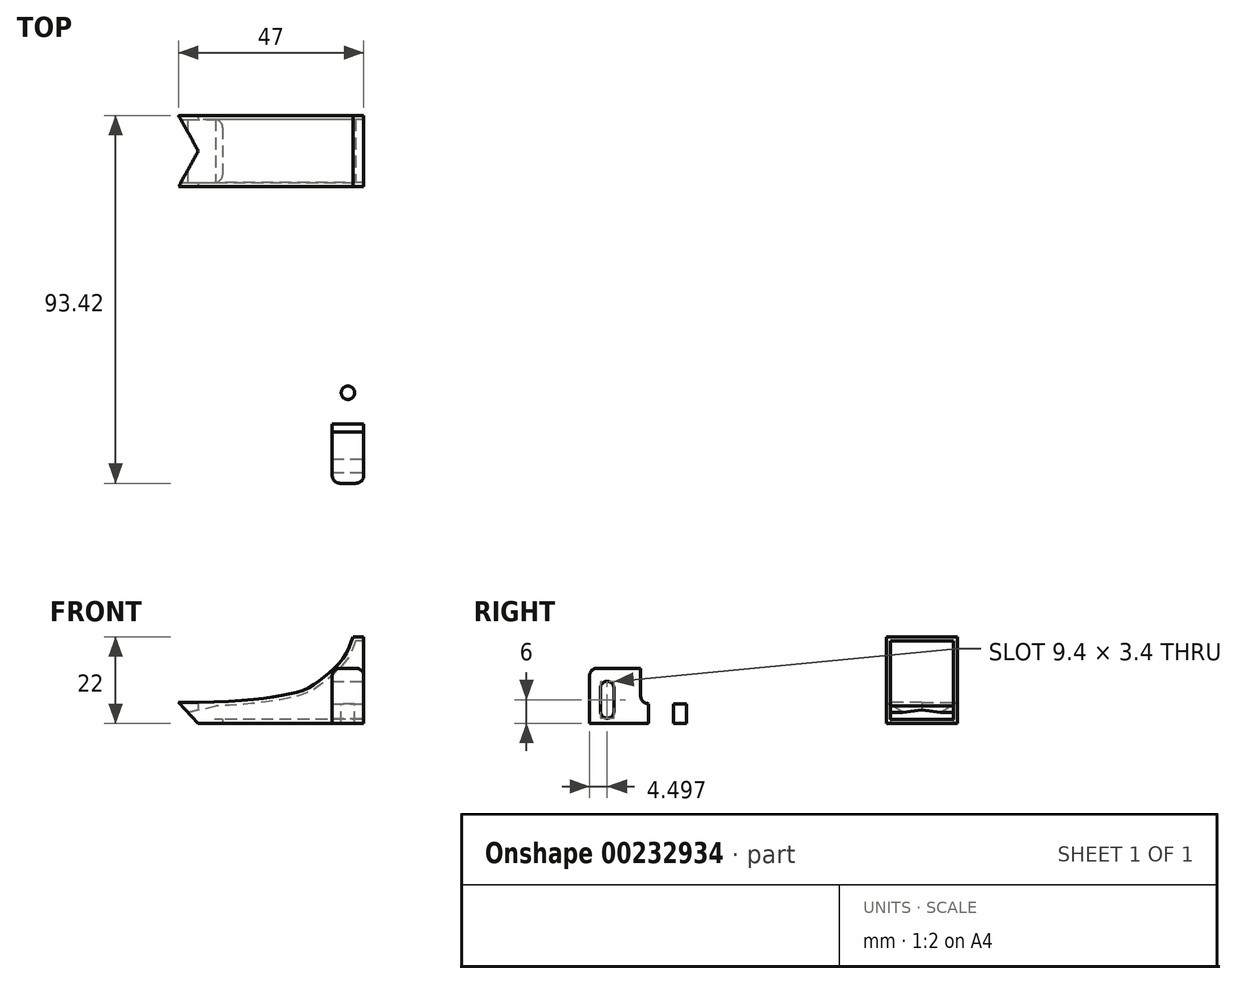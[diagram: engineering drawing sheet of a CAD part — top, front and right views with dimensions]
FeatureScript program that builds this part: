
annotation { "Feature Type Name" : "Feature", "Feature Type Description" : "" }
export const myFeature = defineFeature(function(context is Context, id is Id, definition is map)
    precondition{}
    {
        {
            var Q0;
            Q0=qCreatedBy(makeId("Top.planeOp"),FACE);
            var sketch = newSketch(context, id + "F0", { "sketchPlane" : qUnion([Q0])});
            skLineSegment(sketch, "E0.bottom", {"start": v(0, 0) * mm, "end": v(-47, 0) * mm});
            skLineSegment(sketch, "E0.top", {"start": v(0, 18) * mm, "end": v(-47, 18) * mm});
            skLineSegment(sketch, "E0.left", {"start": v(0, 0) * mm, "end": v(0, 18) * mm});
            skLineSegment(sketch, "E0.right", {"start": v(-47, 0) * mm, "end": v(-47, 18) * mm});
            skSolve(sketch);
        }
        {
            var Q0;
            Q0=makeQuery(id+"F0.imprint","IMPRINT",FACE,{"disambiguationData":[TD([[makeQuery(id+"F0.imprint","IMPRINT",EDGE,{"derivedFrom":sQuery(id+"F0.wireOp",EDGE,"E0.bottom")}),-1.0]])]});
            extrude(context, id + "F1", {"entities" : qUnion([Q0]), "depth" : 22 * mm});
        }
        {
            var Q0;
            Q0=makeQuery(id+"F1.opExtrude","SWEPT_FACE",FACE,{"disambiguationData":[OSD([sQuery(id+"F0.wireOp",EDGE,"E0.left")])]});
            var sketch = newSketch(context, id + "F2", { "sketchPlane" : qUnion([Q0])});
            skLineSegment(sketch, "E1.0", {"start": v(1, 21) * mm, "end": v(1, 1) * mm});
            skLineSegment(sketch, "E1.1", {"start": v(1, 21) * mm, "end": v(17, 21) * mm});
            skLineSegment(sketch, "E1.2", {"start": v(17, 21) * mm, "end": v(17, 1) * mm});
            skLineSegment(sketch, "E1.3", {"start": v(1, 1) * mm, "end": v(17, 1) * mm});
            skSolve(sketch);
        }
        {
            var Q0;
            Q0=makeQuery(id+"F1.opExtrude","SWEPT_FACE",FACE,{"disambiguationData":[OSD([sQuery(id+"F0.wireOp",EDGE,"E0.bottom")])]});
            var sketch = newSketch(context, id + "F3", { "sketchPlane" : qUnion([Q0])});
            skFitSpline(sketch, "E2", {"points": [v(-2.69, 22) * mm, v(-4.67, 17.3) * mm, v(-9.36, 12.4) * mm, v(-14.06, 9) * mm, v(-21.54, 6.98) * mm, v(-47, 5.31) * mm], "startDerivative": vector(-11.82, -27.31) * mm, "endDerivative": vector(-115.84, 1.02) * mm});
            skLineSegment(sketch, "E3", {"start": v(-47, 5.31) * mm, "end": v(-42, 0) * mm});
            skSolve(sketch);
        }
        {
            var Q0;
            {var subQ0=sQuery(id+"F3.wireOp",EDGE,"E2");Q0=makeQuery(id+"F3.imprint","IMPRINT",FACE,{"disambiguationData":[TD([[makeQuery(id+"F3.imprint","IMPRINT",EDGE,{"derivedFrom":subQ0}),-1.0]])]});}
            extrude(context, id + "F4", {"entities" : qUnion([Q0]), "operationType" : NewBodyOperationType.REMOVE, "oppositeDirection" : true, "depth" : 25 * mm});
        }
        {
            var Q0;
            {var subQ0=sQuery(id+"F3.wireOp",EDGE,"E3");Q0=makeQuery(id+"F3.imprint","IMPRINT",FACE,{"disambiguationData":[TD([[makeQuery(id+"F3.imprint","IMPRINT",EDGE,{"derivedFrom":subQ0}),-1.0]])]});}
            extrude(context, id + "F5", {"entities" : qUnion([Q0]), "operationType" : NewBodyOperationType.REMOVE, "oppositeDirection" : true, "depth" : 25 * mm});
        }
        {
            var Q0;
            Q0=makeQuery(id+"F5.boolean.opBoolean","COPY",FACE,{"derivedFrom":makeQuery(id+"F5.opExtrude","SWEPT_FACE",FACE,{"disambiguationData":[OSD([sQuery(id+"F3.wireOp",EDGE,"E3")])]})});
            var sketch = newSketch(context, id + "F6", { "sketchPlane" : qUnion([Q0])});
            skPoint(sketch, "E4", {"position": v(-17, 35.08) * mm});
            skPoint(sketch, "E5", {"position": v(-1, 29.78) * mm});
            skLineSegment(sketch, "E6.bottom", {"start": v(-17, 35.08) * mm, "end": v(-1, 35.08) * mm});
            skLineSegment(sketch, "E6.top", {"start": v(-17, 29.78) * mm, "end": v(-1, 29.78) * mm});
            skLineSegment(sketch, "E6.left", {"start": v(-17, 35.08) * mm, "end": v(-17, 29.78) * mm});
            skLineSegment(sketch, "E6.right", {"start": v(-1, 35.08) * mm, "end": v(-1, 29.78) * mm});
            skSolve(sketch);
        }
        {
            var Q0;
            Q0=makeQuery(id+"F5.boolean.opBoolean","COPY",FACE,{"derivedFrom":makeQuery(id+"F5.opExtrude","SWEPT_FACE",FACE,{"disambiguationData":[OSD([sQuery(id+"F3.wireOp",EDGE,"E3")])]})});
            shell(context, id + "F7", {"entities" : qUnion([Q0]), "thickness" : 1 * mm});
        }
        {
            var Q0;
            Q0=makeQuery(id+"F2.imprint","IMPRINT",FACE,{"disambiguationData":[TD([[makeQuery(id+"F2.imprint","IMPRINT",EDGE,{"derivedFrom":sQuery(id+"F2.wireOp",EDGE,"E1.0")}),1.0]])]});
            extrude(context, id + "F8", {"entities" : qUnion([Q0]), "operationType" : NewBodyOperationType.REMOVE, "oppositeDirection" : true, "depth" : 1 * mm});
        }
        {
            var Q0;
            Q0=qCreatedBy(makeId("Top.planeOp"),FACE);
            var sketch = newSketch(context, id + "F9", { "sketchPlane" : qUnion([Q0])});
            skLineSegment(sketch, "E7.bottom", {"start": v(0, -49.42) * mm, "end": v(-8, -49.42) * mm});
            skLineSegment(sketch, "E7.top", {"start": v(0, -75.42) * mm, "end": v(-8, -75.42) * mm});
            skLineSegment(sketch, "E7.left", {"start": v(0, -49.42) * mm, "end": v(0, -75.42) * mm});
            skLineSegment(sketch, "E7.right", {"start": v(-8, -49.42) * mm, "end": v(-8, -75.42) * mm});
            skSolve(sketch);
        }
        {
            var Q0;
            Q0=makeQuery(id+"F9.imprint","IMPRINT",FACE,{"disambiguationData":[TD([[makeQuery(id+"F9.imprint","IMPRINT",EDGE,{"derivedFrom":sQuery(id+"F9.wireOp",EDGE,"E7.bottom")}),1.0]])]});
            extrude(context, id + "F10", {"entities" : qUnion([Q0]), "depth" : 14 * mm});
        }
        {
            var Q0;
            Q0=makeQuery(id+"F10.opExtrude","SWEPT_FACE",FACE,{"disambiguationData":[OSD([sQuery(id+"F9.wireOp",EDGE,"E7.left")])]});
            var sketch = newSketch(context, id + "F11", { "sketchPlane" : qUnion([Q0])});
            skLineSegment(sketch, "E8", {"start": v(-62.42, 14) * mm, "end": v(-62.42, 5) * mm});
            skLineSegment(sketch, "E9", {"start": v(-62.42, 5) * mm, "end": v(-49.42, 5) * mm});
            skSolve(sketch);
        }
        {
            var Q0;
            {var subQ0=sQuery(id+"F11.wireOp",EDGE,"E8");Q0=makeQuery(id+"F11.imprint","IMPRINT",FACE,{"disambiguationData":[TD([[makeQuery(id+"F11.imprint","IMPRINT",EDGE,{"derivedFrom":subQ0}),1.0]])]});}
            extrude(context, id + "F12", {"entities" : qUnion([Q0]), "operationType" : NewBodyOperationType.REMOVE, "oppositeDirection" : true, "depth" : 25 * mm});
        }
        {
            var Q0;
            Q0=makeQuery(id+"F10.opExtrude","CAP_EDGE",EDGE,{"disambiguationData":[OSD([sQuery(id+"F9.wireOp",EDGE,"E7.top")])],"isStart":false});
            var Q1;
            Q1=makeQuery(id+"F10.opExtrude","SWEPT_EDGE",EDGE,{"disambiguationData":[OSD([sQuery(id+"F9.wireOp",EDGE,"E7.top"),sQuery(id+"F9.wireOp",EDGE,"E7.right")])]});
            var Q2;
            Q2=makeQuery(id+"F10.opExtrude","SWEPT_EDGE",EDGE,{"disambiguationData":[OSD([sQuery(id+"F9.wireOp",EDGE,"E7.top"),sQuery(id+"F9.wireOp",EDGE,"E7.left")])]});
            var Q3;
            Q3=makeQuery(id+"F10.opExtrude","CAP_EDGE",EDGE,{"disambiguationData":[OSD([sQuery(id+"F9.wireOp",EDGE,"E7.left")])],"isStart":false});
            var Q4;
            Q4=makeQuery(id+"F10.opExtrude","CAP_EDGE",EDGE,{"disambiguationData":[OSD([sQuery(id+"F9.wireOp",EDGE,"E7.right")])],"isStart":false});
            var Q5;
            Q5=makeQuery(id+"F12.boolean.opBoolean","COPY",EDGE,{"derivedFrom":makeQuery(id+"F12.opExtrude","SWEPT_EDGE",EDGE,{"disambiguationData":[OSD([sQuery(id+"F11.wireOp",EDGE,"E8"),sQuery(id+"F11.wireOp",EDGE,"E9")])]})});
            var Q6;
            Q6=makeQuery(id+"F10.opExtrude","SWEPT_EDGE",EDGE,{"disambiguationData":[OSD([sQuery(id+"F9.wireOp",EDGE,"E7.bottom"),sQuery(id+"F9.wireOp",EDGE,"E7.left")])]});
            var Q7;
            Q7=makeQuery(id+"F10.opExtrude","SWEPT_EDGE",EDGE,{"disambiguationData":[OSD([sQuery(id+"F9.wireOp",EDGE,"E7.bottom"),sQuery(id+"F9.wireOp",EDGE,"E7.right")])]});
            var Q8;
            Q8=makeQuery(id+"F12.boolean.opBoolean","COPY",EDGE,{"derivedFrom":makeQuery(id+"F12.opExtrude","SWEPT_EDGE",EDGE,{"disambiguationData":[OSD([sQuery(id+"F9.wireOp",EDGE,"E7.left"),sQuery(id+"F11.wireOp",EDGE,"E8")])]})});
            fillet(context, id + "F13", {"entities" : qUnion([Q0, Q1, Q2, Q3, Q4, Q5, Q6, Q7, Q8]), "radius" : 2 * mm, "tangentPropagation" : true, "allowEdgeOverflow" : false});
        }
        {
            var Q0;
            Q0=makeQuery(id+"F10.opExtrude","SWEPT_FACE",FACE,{"disambiguationData":[OSD([sQuery(id+"F9.wireOp",EDGE,"E7.left")])]});
            var sketch = newSketch(context, id + "F14", { "sketchPlane" : qUnion([Q0])});
            skPoint(sketch, "E10", {"position": v(-70.92, 9) * mm});
            skPoint(sketch, "E11", {"position": v(-70.92, 3) * mm});
            skCircle(sketch, "E12", {"center": v(-70.92, 3) * mm, "radius": 1.7 * mm});
            skCircle(sketch, "E13", {"center": v(-70.92, 9) * mm, "radius": 1.7 * mm});
            skLineSegment(sketch, "E14", {"start": v(-72.62, 9) * mm, "end": v(-72.62, 3) * mm});
            skLineSegment(sketch, "E15", {"start": v(-69.22, 9) * mm, "end": v(-69.22, 3) * mm});
            skSolve(sketch);
        }
        {
            var Q0;
            {var subQ0=sQuery(id+"F14.wireOp",EDGE,"E14");Q0=makeQuery(id+"F14.imprint","IMPRINT",FACE,{"disambiguationData":[TD([[makeQuery(id+"F14.imprint","IMPRINT",EDGE,{"derivedFrom":subQ0}),1.0]])]});}
            var Q1;
            {var subQ0=sQuery(id+"F14.wireOp",EDGE,"E13");var subQ1=makeQuery(id+"F14.imprint","INTERSECT",VERTEX,{"derivedFrom":[subQ0,sQuery(id+"F14.wireOp",EDGE,"E14")]});Q1=makeQuery(id+"F14.imprint","IMPRINT",FACE,{"disambiguationData":[TD([[makeQuery(id+"F14.imprint","IMPRINT",EDGE,{"disambiguationData":[TD([[subQ1,1.0]])],"derivedFrom":subQ0}),1.0]])]});}
            var Q2;
            {var subQ0=sQuery(id+"F14.wireOp",EDGE,"E12");var subQ1=makeQuery(id+"F14.imprint","INTERSECT",VERTEX,{"derivedFrom":[subQ0,sQuery(id+"F14.wireOp",EDGE,"E14")]});Q2=makeQuery(id+"F14.imprint","IMPRINT",FACE,{"disambiguationData":[TD([[makeQuery(id+"F14.imprint","IMPRINT",EDGE,{"disambiguationData":[TD([[subQ1,1.0]])],"derivedFrom":subQ0}),1.0]])]});}
            extrude(context, id + "F15", {"entities" : qUnion([Q0, Q1, Q2]), "operationType" : NewBodyOperationType.REMOVE, "oppositeDirection" : true, "depth" : 25 * mm});
        }
        {
            var Q0;
            Q0=makeQuery(id+"F12.boolean.opBoolean","COPY",FACE,{"derivedFrom":makeQuery(id+"F12.opExtrude","SWEPT_FACE",FACE,{"disambiguationData":[OSD([sQuery(id+"F11.wireOp",EDGE,"E9")])]})});
            var sketch = newSketch(context, id + "F16", { "sketchPlane" : qUnion([Q0])});
            skLineSegment(sketch, "E16", {"start": v(-8, -51.42) * mm, "end": v(0, -51.42) * mm});
            skCircle(sketch, "E17", {"center": v(-4, -52.42) * mm, "radius": 1.7 * mm});
            skPoint(sketch, "E17.centerSnap0", {"position": v(-4, -51.42) * mm});
            skSolve(sketch);
        }
        {
            var Q0;
            {var subQ0=sQuery(id+"F16.wireOp",EDGE,"E17");var subQ1=sQuery(id+"F16.wireOp",EDGE,"E16");var subQ2=makeQuery(id+"F16.imprint","INTERSECT",VERTEX,{"disambiguationData":[OD(0.0)],"derivedFrom":[subQ1,subQ0]});Q0=makeQuery(id+"F16.imprint","IMPRINT",FACE,{"disambiguationData":[TD([[makeQuery(id+"F16.imprint","IMPRINT",EDGE,{"disambiguationData":[TD([[subQ2,-1.0]])],"derivedFrom":subQ1}),-1.0]])]});}
            var Q1;
            {var subQ0=sQuery(id+"F16.wireOp",EDGE,"E17");var subQ1=sQuery(id+"F16.wireOp",EDGE,"E16");var subQ2=makeQuery(id+"F16.imprint","INTERSECT",VERTEX,{"disambiguationData":[OD(0.0)],"derivedFrom":[subQ1,subQ0]});Q1=makeQuery(id+"F16.imprint","IMPRINT",FACE,{"disambiguationData":[TD([[makeQuery(id+"F16.imprint","IMPRINT",EDGE,{"disambiguationData":[TD([[subQ2,-1.0]])],"derivedFrom":subQ1}),1.0]])]});}
            extrude(context, id + "F17", {"entities" : qUnion([Q0, Q1]), "operationType" : NewBodyOperationType.REMOVE, "oppositeDirection" : true, "depth" : 25 * mm});
        }
        {
            var Q0;
            Q0=makeQuery(id+"F1.opExtrude","CAP_FACE",FACE,{"disambiguationData":[OSD([sQuery(id+"F0.wireOp",EDGE,"E0.bottom"),sQuery(id+"F0.wireOp",EDGE,"E0.top"),sQuery(id+"F0.wireOp",EDGE,"E0.left"),sQuery(id+"F0.wireOp",EDGE,"E0.right")])],"isStart":true});
            var sketch = newSketch(context, id + "F18", { "sketchPlane" : qUnion([Q0])});
            skPoint(sketch, "E18.centerSnap0", {"position": v(-42, -9) * mm});
            skPoint(sketch, "E19.0", {"position": v(-46.31, -17) * mm});
            skPoint(sketch, "E20.0", {"position": v(-46.31, -1) * mm});
            skLineSegment(sketch, "E21", {"start": v(-46.31, -17) * mm, "end": v(-49.62, -21.75) * mm});
            skLineSegment(sketch, "E22", {"start": v(-46.31, -1) * mm, "end": v(-48.86, 2.72) * mm});
            skLineSegment(sketch, "E23", {"start": v(-48.86, 2.72) * mm, "end": v(-49.62, -21.75) * mm});
            skPoint(sketch, "E24.0", {"position": v(-47, 0) * mm});
            skPoint(sketch, "E25.0", {"position": v(-47, -18) * mm});
            skLineSegment(sketch, "E26", {"start": v(-47, 0) * mm, "end": v(-42, -9) * mm});
            skLineSegment(sketch, "E27", {"start": v(-47, -18) * mm, "end": v(-42, -9) * mm});
            skLineSegment(sketch, "E28", {"start": v(-47, 0) * mm, "end": v(-47, -18) * mm});
            skSolve(sketch);
        }
        {
            var Q0;
            Q0=makeQuery(id+"F1.opExtrude","CAP_FACE",FACE,{"disambiguationData":[OSD([sQuery(id+"F0.wireOp",EDGE,"E0.bottom"),sQuery(id+"F0.wireOp",EDGE,"E0.top"),sQuery(id+"F0.wireOp",EDGE,"E0.left"),sQuery(id+"F0.wireOp",EDGE,"E0.right")])],"isStart":true});
            var sketch = newSketch(context, id + "F19", { "sketchPlane" : qUnion([Q0])});
            skPoint(sketch, "E29.0", {"position": v(-42.69, -17) * mm});
            skPoint(sketch, "E30.0", {"position": v(-42.69, -1) * mm});
            skLineSegment(sketch, "E31", {"start": v(-42.69, -1) * mm, "end": v(-35.86, -1) * mm});
            skLineSegment(sketch, "E32", {"start": v(-35.86, -1) * mm, "end": v(-35.86, -17) * mm});
            skLineSegment(sketch, "E33", {"start": v(-35.86, -17) * mm, "end": v(-42.69, -17) * mm});
            skLineSegment(sketch, "E34", {"start": v(-43.1, -17) * mm, "end": v(-42.69, -17) * mm});
            skLineSegment(sketch, "E35", {"start": v(-43.1, -17) * mm, "end": v(-43.1, -1) * mm});
            skLineSegment(sketch, "E36", {"start": v(-43.1, -1) * mm, "end": v(-42.69, -1) * mm});
            skSolve(sketch);
        }
        {
            var Q0;
            {var subQ1=sQuery(id+"F19.wireOp",EDGE,"E32");Q0=makeQuery(id+"F19.imprint","IMPRINT",FACE,{"disambiguationData":[TD([[makeQuery(id+"F19.imprint","IMPRINT",EDGE,{"derivedFrom":subQ1}),-1.0]])]});}
            var Q1;
            {var subQ0=sQuery(id+"F19.wireOp",EDGE,"E34");Q1=makeQuery(id+"F19.imprint","IMPRINT",FACE,{"disambiguationData":[TD([[makeQuery(id+"F19.imprint","IMPRINT",EDGE,{"derivedFrom":subQ0}),1.0]])]});}
            extrude(context, id + "F20", {"entities" : qUnion([Q0, Q1]), "operationType" : NewBodyOperationType.REMOVE, "oppositeDirection" : true, "depth" : 2 * mm});
        }
        {
            var Q0;
            Q0=makeQuery(id+"F20.boolean.opBoolean","COPY",EDGE,{"derivedFrom":makeQuery(id+"F20.opExtrude","SWEPT_EDGE",EDGE,{"disambiguationData":[OSD([sQuery(id+"F19.wireOp",EDGE,"E32"),sQuery(id+"F19.wireOp",EDGE,"E33")])]})});
            var Q1;
            Q1=makeQuery(id+"F20.boolean.opBoolean","COPY",EDGE,{"derivedFrom":makeQuery(id+"F20.opExtrude","SWEPT_EDGE",EDGE,{"disambiguationData":[OSD([sQuery(id+"F19.wireOp",EDGE,"E31"),sQuery(id+"F19.wireOp",EDGE,"E32")])]})});
            var Q2;
            {var subQ0=sQuery(id+"F3.wireOp",EDGE,"E3");var subQ1=sQuery(id+"F0.wireOp",EDGE,"E0.top");var subQ2=sQuery(id+"F0.wireOp",EDGE,"E0.bottom");Q2=makeQuery(id+"F3cUzVPnUdzeMXx_2.boolean.opBoolean","SPLIT",EDGE,{"disambiguationData":[TD([makeQuery(id+"F1.opExtrude","SWEPT_FACE",FACE,{"disambiguationData":[OSD([subQ1])]})])],"derivedFrom":makeQuery(id+"F5.boolean.opBoolean","COPY",EDGE,{"derivedFrom":makeQuery(id+"F5.opExtrude","SWEPT_EDGE",EDGE,{"disambiguationData":[OSD([subQ2,subQ0])]})})});}
            var Q3;
            {var subQ0=sQuery(id+"F3.wireOp",EDGE,"E3");var subQ1=sQuery(id+"F0.wireOp",EDGE,"E0.bottom");Q3=makeQuery(id+"F3cUzVPnUdzeMXx_2.boolean.opBoolean","SPLIT",EDGE,{"disambiguationData":[TD([makeQuery(id+"F1.opExtrude","SWEPT_FACE",FACE,{"disambiguationData":[OSD([subQ1])]})])],"derivedFrom":makeQuery(id+"F5.boolean.opBoolean","COPY",EDGE,{"derivedFrom":makeQuery(id+"F5.opExtrude","SWEPT_EDGE",EDGE,{"disambiguationData":[OSD([subQ1,subQ0])]})})});}
            var Q4;
            Q4=makeQuery(id+"F3cUzVPnUdzeMXx_2.boolean.opBoolean","INTERSECT",EDGE,{"disambiguationData":[OD(0.0)],"derivedFrom":[makeQuery(id+"F5.boolean.opBoolean","COPY",FACE,{"derivedFrom":makeQuery(id+"F5.opExtrude","SWEPT_FACE",FACE,{"disambiguationData":[OSD([sQuery(id+"F3.wireOp",EDGE,"E3")])]})}),makeQuery(id+"F3cUzVPnUdzeMXx_2.opExtrude","SWEPT_FACE",FACE,{"disambiguationData":[OSD([sQuery(id+"F18.wireOp",EDGE,"E27")])]})]});
            var Q5;
            Q5=makeQuery(id+"F3cUzVPnUdzeMXx_2.boolean.opBoolean","INTERSECT",EDGE,{"disambiguationData":[OD(0.0)],"derivedFrom":[makeQuery(id+"F5.boolean.opBoolean","COPY",FACE,{"derivedFrom":makeQuery(id+"F5.opExtrude","SWEPT_FACE",FACE,{"disambiguationData":[OSD([sQuery(id+"F3.wireOp",EDGE,"E3")])]})}),makeQuery(id+"F3cUzVPnUdzeMXx_2.opExtrude","SWEPT_FACE",FACE,{"disambiguationData":[OSD([sQuery(id+"F18.wireOp",EDGE,"E26")])]})]});
            fillet(context, id + "F21", {"entities" : qUnion([Q0, Q1, Q2, Q3, Q4, Q5]), "radius" : 2 * mm, "tangentPropagation" : true, "allowEdgeOverflow" : false});
        }
        {
            var Q0;
            Q0=makeQuery(id+"F20.boolean.opBoolean","MERGE",FACE,{"derivedFrom":[makeQuery(id+"F8.boolean.opBoolean","MERGE",FACE,{"derivedFrom":[makeQuery(id+"F7.opShell","OFFSET_FACE",FACE,{"disambiguationData":[OSD([sQuery(id+"F0.wireOp",EDGE,"E0.top")])]}),makeQuery(id+"F8.opExtrude","SWEPT_FACE",FACE,{"disambiguationData":[OSD([sQuery(id+"F2.wireOp",EDGE,"E1.2")])]})]}),makeQuery(id+"F20.opExtrude","SWEPT_FACE",FACE,{"disambiguationData":[OSD([sQuery(id+"F19.wireOp",EDGE,"E33"),sQuery(id+"F19.wireOp",EDGE,"E34")])]})]});
            var sketch = newSketch(context, id + "F22", { "sketchPlane" : qUnion([Q0])});
            skLineSegment(sketch, "E37", {"start": v(-45.98, 4.3) * mm, "end": v(-44.65, 2.81) * mm});
            skLineSegment(sketch, "E38", {"start": v(-44.65, 2.81) * mm, "end": v(-37.62, 4.42) * mm});
            skSolve(sketch);
        }
        {
            var Q0;
            {var subQ0=sQuery(id+"F22.wireOp",EDGE,"E37");Q0=makeQuery(id+"F22.imprint","IMPRINT",FACE,{"disambiguationData":[TD([[makeQuery(id+"F22.imprint","IMPRINT",EDGE,{"derivedFrom":subQ0}),1.0]])]});}
            extrude(context, id + "F23", {"entities" : qUnion([Q0]), "operationType" : NewBodyOperationType.ADD, "endBound" : BoundingType.UP_TO_NEXT, "depth" : 20 * mm});
        }
        {
            var Q0;
            {var subQ5=sQuery(id+"F18.wireOp",EDGE,"E26");Q0=makeQuery(id+"F18.imprint","IMPRINT",FACE,{"disambiguationData":[TD([[makeQuery(id+"F18.imprint","IMPRINT",EDGE,{"derivedFrom":subQ5}),-1.0]])]});}
            extrude(context, id + "F24", {"entities" : qUnion([Q0]), "operationType" : NewBodyOperationType.REMOVE, "oppositeDirection" : true, "depth" : 25 * mm});
        }
    });
